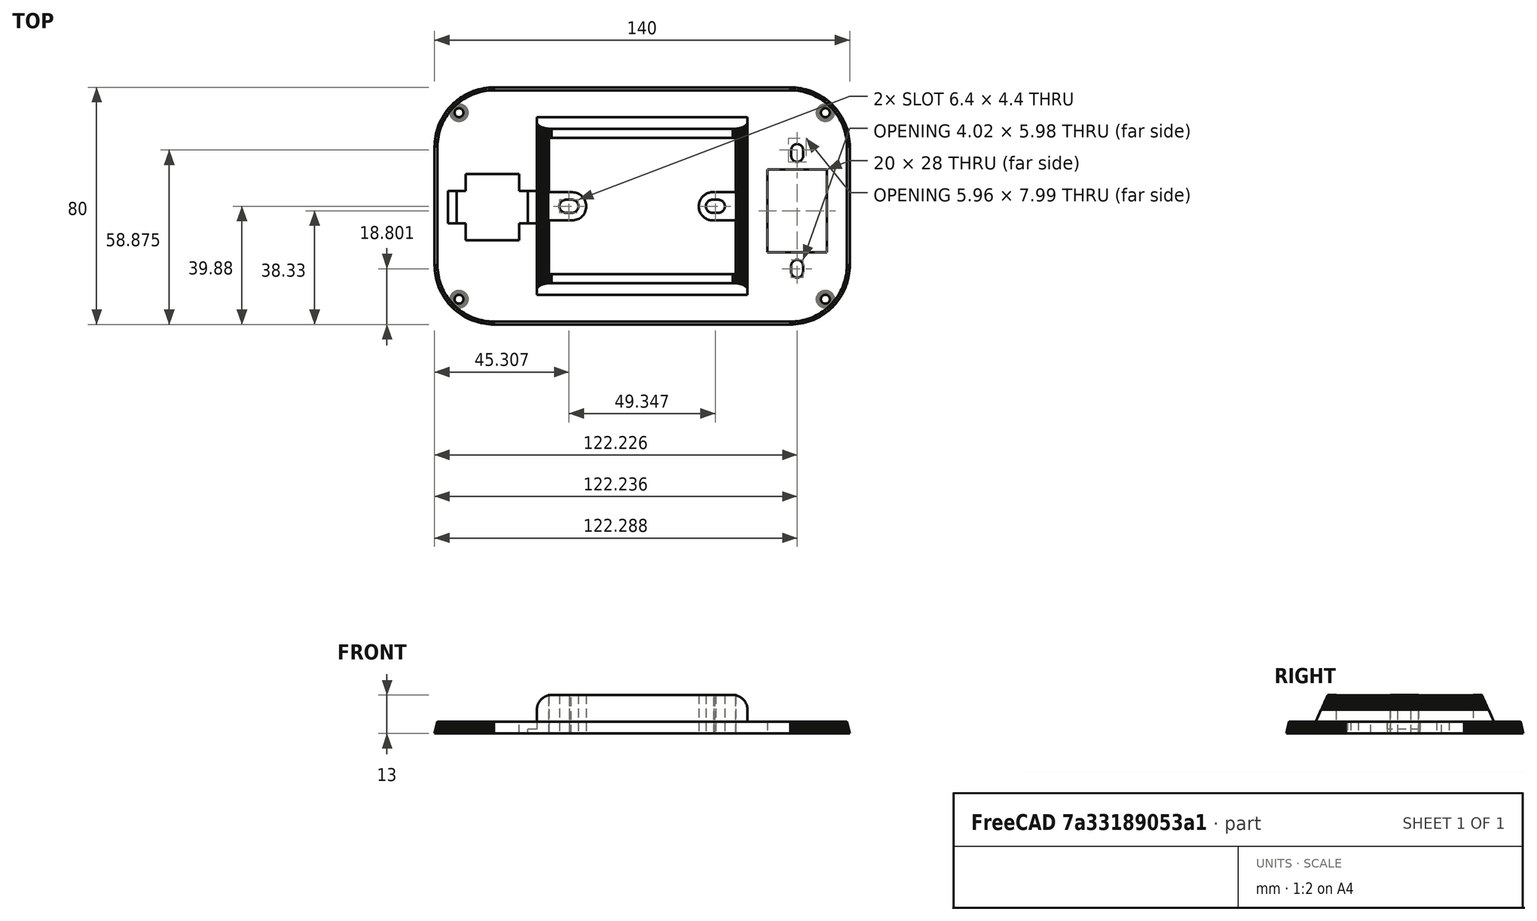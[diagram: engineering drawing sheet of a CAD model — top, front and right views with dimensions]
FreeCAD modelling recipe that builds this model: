
FCSTD DOCUMENT  (FreeCAD 0.18R16093 +53 (Git))
Label: PID Rear
License: All rights reserved
LicenseURL: http://en.wikipedia.org/wiki/All_rights_reserved
objects: Sketcher::SketchObject×4, PartDesign::Pad×2, PartDesign::Pocket×2, Part::Feature×1, PartDesign::Body×1, Mesh::Feature×1
note: 14 computed .brp shape members not serialized (recipe doc carries the construction recipe); baked Part::Feature solids carry a one-line shape summary decoded from their .brp

FEATURE [Part::Feature] Solid
  shape: bbox 140 x 80 x 13 mm, 3159 faces (baked)
FEATURE [Sketcher::SketchObject] Sketch
  MapMode = 5
  Placement = pos=(0,0,0) rot=(1,0,0;3.14159rad)
  Support = -> [Solid]
  sketch-geometry (10):
    g0: ArcOfCircle CenterX=59.3456 CenterY=20.068 CenterZ=0 NormalX=0 NormalY=0 NormalZ=1 AngleXU=0 Radius=2 StartAngle=3.14159 EndAngle=6.28319
    g1: ArcOfCircle CenterX=59.3456 CenterY=22.068 CenterZ=0 NormalX=0 NormalY=0 NormalZ=1 AngleXU=0 Radius=2 StartAngle=2e-16 EndAngle=3.14159
    g2: LineSegment StartX=61.3456 StartY=20.068 StartZ=0 EndX=61.3456 EndY=22.068 EndZ=0
    g3: LineSegment StartX=57.3456 StartY=20.068 StartZ=0 EndX=57.3456 EndY=22.068 EndZ=0
    g4: ArcOfCircle CenterX=59.3837 CenterY=-19.0001 CenterZ=0 NormalX=0 NormalY=0 NormalZ=1 AngleXU=0 Radius=2 StartAngle=3.14159 EndAngle=6.28319
    g5: ArcOfCircle CenterX=59.3837 CenterY=-17.0001 CenterZ=0 NormalX=0 NormalY=0 NormalZ=1 AngleXU=0 Radius=2 StartAngle=4e-16 EndAngle=3.14159
    g6: LineSegment StartX=61.3837 StartY=-19.0001 StartZ=0 EndX=61.3837 EndY=-17.0001 EndZ=0
    g7: LineSegment StartX=57.3837 StartY=-19.0001 StartZ=0 EndX=57.3837 EndY=-17.0001 EndZ=0
    g8: LineSegment StartX=49.3394 StartY=15.5668 StartZ=0 EndX=69.3037 EndY=15.5692 EndZ=0
    g9: LineSegment [constr] StartX=49.3129 StartY=-12.4991 StartZ=0 EndX=69.4065 EndY=-12.5011 EndZ=0
  constraints (26):
    c: Tangent(g0,g3) = 1.5708
    c: Tangent(g0,g2) = -1.5708
    c: Tangent(g2,g1) = -1.5708
    c: Tangent(g3,g1) = 1.5708
    c: Vertical(g2)
    c: Equal(g0,g1)
    c: Radius(g0) = 2
    c: Tangent(g4,g7) = 1.5708
    c: Tangent(g4,g6) = -1.5708
    c: Tangent(g6,g5) = -1.5708
    c: Tangent(g7,g5) = 1.5708
    c: Vertical(g6)
    c: Equal(g4,g5)
    c: Radius(g5) = 2
    c: Distance(g5,g4) = 2
    c: Distance(g0,g1) = 2
    c: Distance(g5,g9) = 4.5
    c: DistanceX(g9) = 69.4065
    c: DistanceY(g9) = -12.5011
    c: DistanceX(g9) = 49.3129
    c: DistanceY(g9) = -12.4991
    c: DistanceX(g8) = 69.3037
    c: DistanceY(g8) = 15.5692
    c: DistanceX(g8) = 49.3394
    c: DistanceY(g8) = 15.5668
    c: Distance(g0,g8) = 4.5
FEATURE [Sketcher::SketchObject] Sketch001
  MapMode = 5
  Placement = pos=(0,0,0) rot=(1,0,0;3.14159rad)
  Support = -> [Solid]
  sketch-geometry (1):
    g0: Circle CenterX=59.3988 CenterY=-20 CenterZ=0 NormalX=0 NormalY=0 NormalZ=1 AngleXU=0 Radius=3
  constraints (1):
    c: Radius(g0) = 3
FEATURE [PartDesign::Pad] Pad
  Length = 10
  Length2 = 100
  Profile = -> Sketch001
  Type = 3
  UpToFace = -> Solid [Face1720]
FEATURE [PartDesign::Pocket] Pocket
  BaseFeature = -> Pad
  Length = 8
  Length2 = 100
  Midplane = true
  Profile = -> Sketch
  Type = 0
FEATURE [Sketcher::SketchObject] Sketch002
  MapMode = 5
  Placement = pos=(0,0,0) rot=(1,0,0;3.14159rad)
  Support = -> [Pocket]
  sketch-geometry (8):
    g0: LineSegment StartX=-16.4815 StartY=4.75 StartZ=0 EndX=-24.5919 EndY=4.75 EndZ=0
    g1: LineSegment StartX=-24.5919 StartY=4.75 StartZ=0 EndX=-24.5919 EndY=-4.75 EndZ=0
    g2: LineSegment StartX=-24.5919 StartY=-4.75 StartZ=0 EndX=-16.4815 EndY=-4.75 EndZ=0
    g3: LineSegment StartX=31.4885 StartY=4.75 StartZ=0 EndX=38.7379 EndY=4.75 EndZ=0
    g4: LineSegment StartX=38.7379 StartY=4.75 StartZ=0 EndX=38.7379 EndY=-4.75 EndZ=0
    g5: LineSegment StartX=38.7379 StartY=-4.75 StartZ=0 EndX=31.4885 EndY=-4.75 EndZ=0
    g6: ArcOfCircle CenterX=30.9849 CenterY=-2e-16 CenterZ=0 NormalX=0 NormalY=0 NormalZ=1 AngleXU=0 Radius=4.77662 StartAngle=1.46518 EndAngle=4.81801
    g7: ArcOfCircle CenterX=-16.4815 CenterY=4e-16 CenterZ=0 NormalX=0 NormalY=0 NormalZ=1 AngleXU=0 Radius=4.75 StartAngle=4.71239 EndAngle=7.85398
  constraints (17):
    c: Horizontal(g0)
    c: Horizontal(g2)
    c: Coincident(g0,g1)
    c: Coincident(g2,g1)
    c: Symmetric(g0,g1,g-1)
    c: Horizontal(g3)
    c: Coincident(g3,g4)
    c: Vertical(g4)
    c: Coincident(g4,g5)
    c: Horizontal(g5)
    c: Coincident(g6,g5)
    c: Coincident(g6,g3)
    c: Symmetric(g3,g5,g-1)
    c: DistanceY(g2,g0) = 9.5
    c: DistanceY(g5,g3) = 9.5
    c: Coincident(g7,g0)
    c: Coincident(g7,g2)
FEATURE [PartDesign::Pad] Pad001
  BaseFeature = -> Pocket
  Length = 13
  Length2 = 100
  Profile = -> Sketch002
  Reversed = true
  Type = 0
FEATURE [Sketcher::SketchObject] Sketch003
  MapMode = 5
  Placement = pos=(0,0,0) rot=(1,0,0;3.14159rad)
  Support = -> [Pad001]
  sketch-geometry (8):
    g0: ArcOfCircle CenterX=-18.5629 CenterY=-2e-16 CenterZ=0 NormalX=0 NormalY=0 NormalZ=1 AngleXU=0 Radius=2.2 StartAngle=1.5708 EndAngle=4.71239
    g1: ArcOfCircle CenterX=-16.5629 CenterY=-1e-16 CenterZ=0 NormalX=0 NormalY=0 NormalZ=1 AngleXU=0 Radius=2.2 StartAngle=4.71239 EndAngle=7.85398
    g2: LineSegment StartX=-18.5629 StartY=-2.2 StartZ=0 EndX=-16.5629 EndY=-2.2 EndZ=0
    g3: LineSegment StartX=-18.5629 StartY=2.2 StartZ=0 EndX=-16.5629 EndY=2.2 EndZ=0
    g4: ArcOfCircle CenterX=32.7844 CenterY=2e-16 CenterZ=0 NormalX=0 NormalY=0 NormalZ=1 AngleXU=0 Radius=2.2 StartAngle=4.71239 EndAngle=7.85398
    g5: ArcOfCircle CenterX=30.7844 CenterY=1e-16 CenterZ=0 NormalX=0 NormalY=0 NormalZ=1 AngleXU=0 Radius=2.2 StartAngle=1.5708 EndAngle=4.71239
    g6: LineSegment StartX=32.7844 StartY=2.2 StartZ=0 EndX=30.7844 EndY=2.2 EndZ=0
    g7: LineSegment StartX=32.7844 StartY=-2.2 StartZ=0 EndX=30.7844 EndY=-2.2 EndZ=0
  constraints (16):
    c: Tangent(g0,g3) = 1.5708
    c: Tangent(g0,g2) = -1.5708
    c: Tangent(g2,g1) = -1.5708
    c: Tangent(g3,g1) = 1.5708
    c: Horizontal(g2)
    c: Symmetric(g1,g1,g-1)
    c: DistanceY(g0,g0) = 4.4
    c: Tangent(g4,g7) = 1.5708
    c: Tangent(g4,g6) = -1.5708
    c: Tangent(g6,g5) = -1.5708
    c: Tangent(g7,g5) = 1.5708
    c: Horizontal(g6)
    c: Symmetric(g5,g5,g-1)
    c: DistanceY(g4,g4) = 4.4
    c: DistanceX(g0,g1) = 2
    c: DistanceX(g5,g4) = 2
FEATURE [PartDesign::Pocket] Pocket001
  BaseFeature = -> Pad001
  Length = 5
  Length2 = 100
  Profile = -> Sketch003
  Type = 1
FEATURE [PartDesign::Body] Body
  Group = -> [Solid,Sketch,Sketch001,Pad,Pocket,Sketch002,Pad001,Sketch003,Pocket001]
  Origin = -> Origin
  Tip = -> Pocket001
FEATURE [Mesh::Feature] Mesh  label="Pocket001 (Meshed)"
